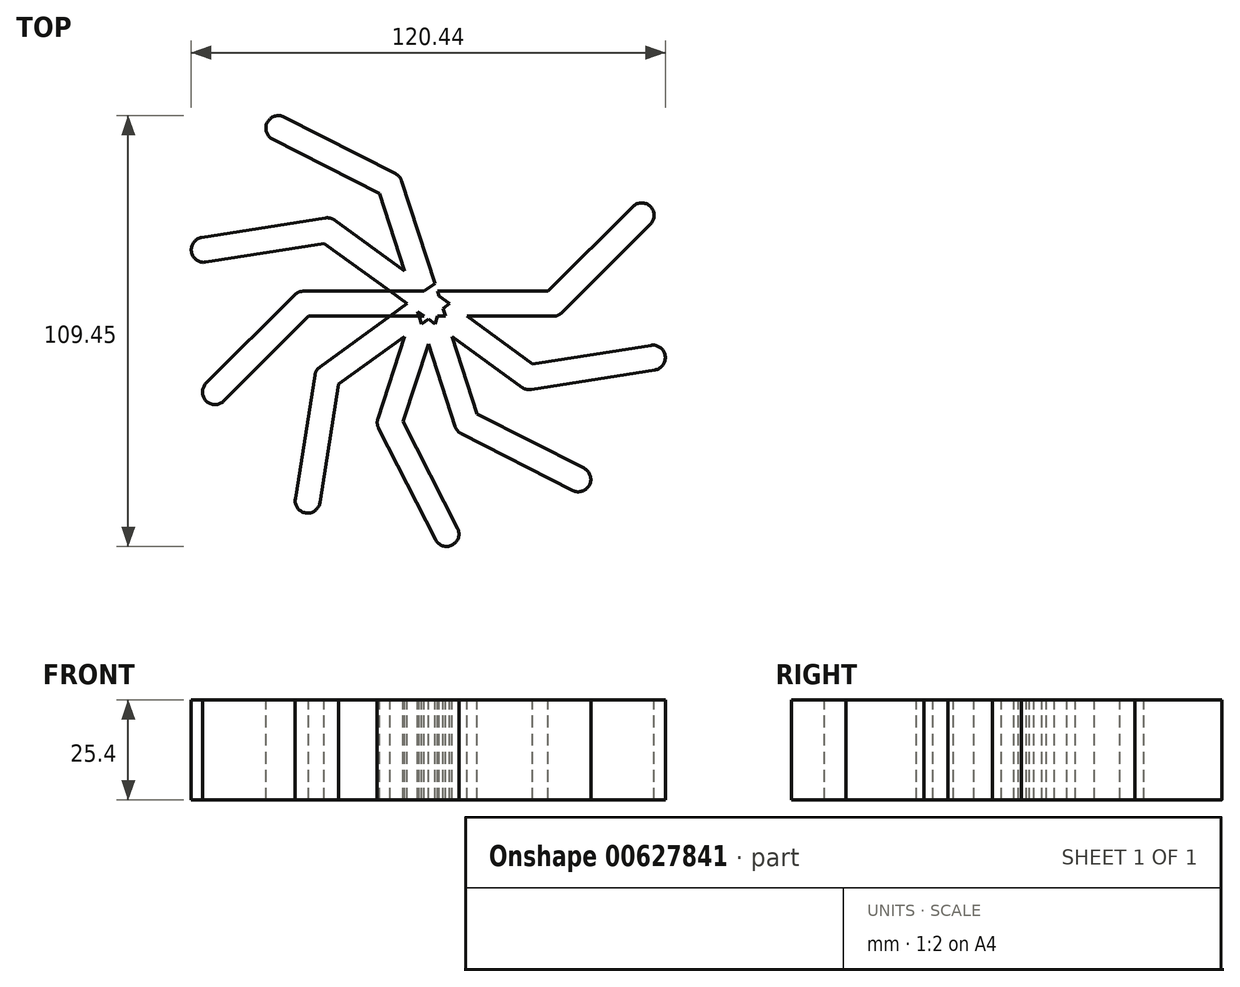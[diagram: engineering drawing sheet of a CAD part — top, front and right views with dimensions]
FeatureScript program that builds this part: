
annotation { "Feature Type Name" : "Feature", "Feature Type Description" : "" }
export const myFeature = defineFeature(function(context is Context, id is Id, definition is map)
    precondition{}
    {
        {
            var Q0;
            Q0=qCreatedBy(makeId("Top.planeOp"),FACE);
            var sketch = newSketch(context, id + "F0", { "sketchPlane" : qUnion([Q0])});
            skArc(sketch, "E0", {"start": v(31.75, -3.18) * mm, "mid": v(32.97, -2.93) * mm, "end": v(34, -2.25) * mm});
            skLineSegment(sketch, "E1", {"start": v(0, 0) * mm, "end": v(31.75, 0) * mm, "construction": true});
            skLineSegment(sketch, "E2", {"start": v(31.75, 0) * mm, "end": v(54.2, 22.45) * mm, "construction": true});
            skArc(sketch, "E3", {"start": v(56.45, 20.2) * mm, "mid": v(56.45, 24.7) * mm, "end": v(51.96, 24.7) * mm});
            skLineSegment(sketch, "E4", {"start": v(0, 3.17) * mm, "end": v(30.43, 3.17) * mm});
            skLineSegment(sketch, "E5", {"start": v(51.96, 24.7) * mm, "end": v(30.43, 3.17) * mm});
            skLineSegment(sketch, "E6", {"start": v(0, -3.18) * mm, "end": v(31.75, -3.18) * mm});
            skLineSegment(sketch, "E7", {"start": v(56.45, 20.2) * mm, "end": v(34, -2.25) * mm});
            skLineSegment(sketch, "E8.1.0", {"start": v(25.69, 18.66) * mm, "end": v(30.65, 50.02) * mm, "construction": true});
            skLineSegment(sketch, "E8.1.1", {"start": v(-1.03, 3.17) * mm, "end": v(22.76, 20.46) * mm});
            skLineSegment(sketch, "E8.1.2", {"start": v(0, 0) * mm, "end": v(25.69, 18.66) * mm, "construction": true});
            skLineSegment(sketch, "E8.1.3", {"start": v(33.79, 49.52) * mm, "end": v(28.82, 18.17) * mm});
            skLineSegment(sketch, "E8.1.4", {"start": v(1.87, -2.57) * mm, "end": v(27.55, 16.1) * mm});
            skLineSegment(sketch, "E8.1.5", {"start": v(27.52, 50.52) * mm, "end": v(22.76, 20.46) * mm});
            skArc(sketch, "E8.1.8", {"start": v(27.55, 16.1) * mm, "mid": v(28.4, 17) * mm, "end": v(28.82, 18.17) * mm});
            skLineSegment(sketch, "E8.2.0", {"start": v(9.81, 30.2) * mm, "end": v(-4.6, 58.49) * mm, "construction": true});
            skLineSegment(sketch, "E8.2.1", {"start": v(-2.7, 1.96) * mm, "end": v(6.39, 29.93) * mm});
            skLineSegment(sketch, "E8.2.2", {"start": v(0.98, 3.02) * mm, "end": v(9.81, 30.2) * mm, "construction": true});
            skLineSegment(sketch, "E8.2.3", {"start": v(-1.77, 59.93) * mm, "end": v(12.64, 31.64) * mm});
            skLineSegment(sketch, "E8.2.4", {"start": v(3.02, -0.98) * mm, "end": v(3.34, 0) * mm});
            skLineSegment(sketch, "E8.2.5", {"start": v(-7.43, 57.04) * mm, "end": v(6.39, 29.93) * mm});
            skArc(sketch, "E8.2.6", {"start": v(-3.02, 0.98) * mm, "mid": v(-0.98, -3.02) * mm, "end": v(3.02, -0.98) * mm});
            skArc(sketch, "E8.2.7", {"start": v(-1.77, 59.93) * mm, "mid": v(-6.04, 61.31) * mm, "end": v(-7.43, 57.04) * mm});
            skArc(sketch, "E8.2.8", {"start": v(12.83, 29.21) * mm, "mid": v(12.98, 30.45) * mm, "end": v(12.64, 31.64) * mm});
            skLineSegment(sketch, "E8.3.0", {"start": v(-9.81, 30.2) * mm, "end": v(-38.1, 44.61) * mm, "construction": true});
            skLineSegment(sketch, "E8.3.2", {"start": v(-0.98, 3.02) * mm, "end": v(-9.81, 30.2) * mm, "construction": true});
            skLineSegment(sketch, "E8.3.3", {"start": v(-36.66, 47.44) * mm, "end": v(-8.37, 33.02) * mm});
            skLineSegment(sketch, "E8.3.4", {"start": v(3.02, 0.98) * mm, "end": v(-6.8, 31.18) * mm});
            skLineSegment(sketch, "E8.3.5", {"start": v(-39.54, 41.78) * mm, "end": v(-12.42, 27.96) * mm});
            skArc(sketch, "E8.3.6", {"start": v(-3.02, -0.98) * mm, "mid": v(0.98, -3.02) * mm, "end": v(3.02, 0.98) * mm});
            skArc(sketch, "E8.3.7", {"start": v(-36.66, 47.44) * mm, "mid": v(-40.93, 46.05) * mm, "end": v(-39.54, 41.78) * mm});
            skArc(sketch, "E8.3.8", {"start": v(-6.8, 31.18) * mm, "mid": v(-7.4, 32.26) * mm, "end": v(-8.37, 33.02) * mm});
            skLineSegment(sketch, "E8.4.0", {"start": v(-25.69, 18.66) * mm, "end": v(-57.05, 13.7) * mm, "construction": true});
            skLineSegment(sketch, "E8.4.1", {"start": v(-1.87, -2.57) * mm, "end": v(-3.73, -1.21) * mm});
            skLineSegment(sketch, "E8.4.2", {"start": v(0, 0) * mm, "end": v(-2.7, 1.96) * mm, "construction": true});
            skLineSegment(sketch, "E8.4.3", {"start": v(-57.54, 16.83) * mm, "end": v(-26.18, 21.8) * mm});
            skLineSegment(sketch, "E8.4.4", {"start": v(1.03, 3.17) * mm, "end": v(-23.82, 21.23) * mm});
            skLineSegment(sketch, "E8.4.5", {"start": v(-56.55, 10.56) * mm, "end": v(-26.49, 15.32) * mm});
            skArc(sketch, "E8.4.6", {"start": v(-1.87, -2.57) * mm, "mid": v(1.44, -2.83) * mm, "end": v(3.18, 0) * mm});
            skArc(sketch, "E8.4.7", {"start": v(-57.54, 16.83) * mm, "mid": v(-60.18, 13.2) * mm, "end": v(-56.55, 10.56) * mm});
            skArc(sketch, "E8.4.8", {"start": v(-23.82, 21.23) * mm, "mid": v(-24.95, 21.75) * mm, "end": v(-26.18, 21.8) * mm});
            skLineSegment(sketch, "E8.5.0", {"start": v(-31.75, 0) * mm, "end": v(-54.2, -22.45) * mm, "construction": true});
            skLineSegment(sketch, "E8.5.1", {"start": v(0, -3.17) * mm, "end": v(-30.43, -3.17) * mm});
            skLineSegment(sketch, "E8.5.2", {"start": v(0, 0) * mm, "end": v(-3.34, 0) * mm, "construction": true});
            skLineSegment(sketch, "E8.5.3", {"start": v(-56.45, -20.2) * mm, "end": v(-34, 2.25) * mm});
            skLineSegment(sketch, "E8.5.4", {"start": v(0, 3.18) * mm, "end": v(-31.75, 3.18) * mm});
            skLineSegment(sketch, "E8.5.5", {"start": v(-51.96, -24.7) * mm, "end": v(-30.43, -3.17) * mm});
            skArc(sketch, "E8.5.6", {"start": v(0, -3.18) * mm, "mid": v(2.25, -2.25) * mm, "end": v(3.18, 0) * mm});
            skArc(sketch, "E8.5.7", {"start": v(-56.45, -20.2) * mm, "mid": v(-56.45, -24.7) * mm, "end": v(-51.96, -24.7) * mm});
            skArc(sketch, "E8.5.8", {"start": v(-31.75, 3.18) * mm, "mid": v(-32.97, 2.93) * mm, "end": v(-34, 2.25) * mm});
            skLineSegment(sketch, "E8.6.0", {"start": v(-25.69, -18.66) * mm, "end": v(-30.65, -50.02) * mm, "construction": true});
            skLineSegment(sketch, "E8.6.1", {"start": v(1.87, -2.57) * mm, "end": v(-22.76, -20.46) * mm});
            skLineSegment(sketch, "E8.6.2", {"start": v(0, 0) * mm, "end": v(-25.69, -18.66) * mm, "construction": true});
            skLineSegment(sketch, "E8.6.3", {"start": v(-33.79, -49.52) * mm, "end": v(-28.82, -18.17) * mm});
            skLineSegment(sketch, "E8.6.5", {"start": v(-27.52, -50.52) * mm, "end": v(-22.76, -20.46) * mm});
            skArc(sketch, "E8.6.6", {"start": v(1.87, -2.57) * mm, "mid": v(2.83, 1.44) * mm, "end": v(-0.98, 3.02) * mm});
            skArc(sketch, "E8.6.7", {"start": v(-33.79, -49.52) * mm, "mid": v(-31.15, -53.16) * mm, "end": v(-27.52, -50.52) * mm});
            skArc(sketch, "E8.6.8", {"start": v(-27.55, -16.1) * mm, "mid": v(-28.4, -17) * mm, "end": v(-28.82, -18.17) * mm});
            skLineSegment(sketch, "E8.7.0", {"start": v(-9.81, -30.2) * mm, "end": v(4.6, -58.49) * mm, "construction": true});
            skLineSegment(sketch, "E8.7.1", {"start": v(3.02, -0.98) * mm, "end": v(-6.39, -29.93) * mm});
            skLineSegment(sketch, "E8.7.2", {"start": v(-0.98, -3.02) * mm, "end": v(-9.81, -30.2) * mm, "construction": true});
            skLineSegment(sketch, "E8.7.3", {"start": v(1.77, -59.93) * mm, "end": v(-12.64, -31.64) * mm});
            skLineSegment(sketch, "E8.7.4", {"start": v(-3.02, 0.98) * mm, "end": v(-3.34, 0) * mm});
            skLineSegment(sketch, "E8.7.5", {"start": v(7.43, -57.04) * mm, "end": v(-6.39, -29.93) * mm});
            skArc(sketch, "E8.7.7", {"start": v(1.77, -59.93) * mm, "mid": v(6.04, -61.31) * mm, "end": v(7.43, -57.04) * mm});
            skArc(sketch, "E8.7.8", {"start": v(-12.83, -29.21) * mm, "mid": v(-12.98, -30.45) * mm, "end": v(-12.64, -31.64) * mm});
            skLineSegment(sketch, "E8.8.0", {"start": v(9.81, -30.2) * mm, "end": v(38.1, -44.61) * mm, "construction": true});
            skLineSegment(sketch, "E8.8.1", {"start": v(3.34, 0) * mm, "end": v(12.42, -27.96) * mm});
            skLineSegment(sketch, "E8.8.2", {"start": v(1.03, -3.18) * mm, "end": v(9.81, -30.2) * mm, "construction": true});
            skLineSegment(sketch, "E8.8.3", {"start": v(36.66, -47.44) * mm, "end": v(8.37, -33.02) * mm});
            skLineSegment(sketch, "E8.8.4", {"start": v(-3.02, -0.98) * mm, "end": v(6.8, -31.18) * mm});
            skLineSegment(sketch, "E8.8.5", {"start": v(39.54, -41.78) * mm, "end": v(12.42, -27.96) * mm});
            skArc(sketch, "E8.8.6", {"start": v(3.02, 0.98) * mm, "mid": v(1.87, 2.57) * mm, "end": v(0, 3.18) * mm});
            skArc(sketch, "E8.8.7", {"start": v(36.66, -47.44) * mm, "mid": v(40.93, -46.05) * mm, "end": v(39.54, -41.78) * mm});
            skArc(sketch, "E8.8.8", {"start": v(6.8, -31.18) * mm, "mid": v(7.4, -32.26) * mm, "end": v(8.37, -33.02) * mm});
            skLineSegment(sketch, "E8.9.0", {"start": v(25.69, -18.66) * mm, "end": v(57.05, -13.7) * mm, "construction": true});
            skLineSegment(sketch, "E8.9.1", {"start": v(1.87, 2.57) * mm, "end": v(26.49, -15.32) * mm});
            skLineSegment(sketch, "E8.9.2", {"start": v(0, 0) * mm, "end": v(25.69, -18.66) * mm, "construction": true});
            skLineSegment(sketch, "E8.9.3", {"start": v(57.54, -16.83) * mm, "end": v(26.18, -21.8) * mm});
            skLineSegment(sketch, "E8.9.4", {"start": v(-1.87, -2.57) * mm, "end": v(23.82, -21.23) * mm});
            skLineSegment(sketch, "E8.9.5", {"start": v(56.55, -10.56) * mm, "end": v(26.49, -15.32) * mm});
            skArc(sketch, "E8.9.6", {"start": v(1.87, 2.57) * mm, "mid": v(0.5, 3.14) * mm, "end": v(-0.98, 3.02) * mm});
            skArc(sketch, "E8.9.7", {"start": v(57.54, -16.83) * mm, "mid": v(60.18, -13.2) * mm, "end": v(56.55, -10.56) * mm});
            skArc(sketch, "E8.9.8", {"start": v(23.82, -21.23) * mm, "mid": v(24.95, -21.75) * mm, "end": v(26.18, -21.8) * mm});
            skPoint(sketch, "E8.center", {"position": v(0, 0) * mm});
            skLineSegment(sketch, "E9.trimOffspring", {"start": v(-5.4, 0) * mm, "end": v(-27.55, -16.1) * mm});
            skLineSegment(sketch, "E10.trimOffspring", {"start": v(-4.37, 3.18) * mm, "end": v(-12.42, 27.96) * mm});
            skLineSegment(sketch, "E11.trimOffspring", {"start": v(-5.4, 0) * mm, "end": v(-31.75, 0) * mm, "construction": true});
            skLineSegment(sketch, "E12.trimOffspring", {"start": v(-6.04, -8.31) * mm, "end": v(-12.83, -29.21) * mm});
            skArc(sketch, "E13.trimOffspring", {"start": v(-3.02, -0.98) * mm, "mid": v(-1.87, -2.57) * mm, "end": v(0, -3.18) * mm});
            skArc(sketch, "E14.trimOffspring", {"start": v(-3.02, 0.98) * mm, "mid": v(-3.14, 0.5) * mm, "end": v(-3.18, 0) * mm});
            skLineSegment(sketch, "E15.trimOffspring", {"start": v(-4.37, 3.17) * mm, "end": v(-25.69, 18.66) * mm, "construction": true});
            skArc(sketch, "E16.trimOffspring", {"start": v(0.98, 3.02) * mm, "mid": v(0.5, 3.14) * mm, "end": v(0, 3.18) * mm});
            skArc(sketch, "E17.trimOffspring", {"start": v(-3.18, 0) * mm, "mid": v(-2.83, -1.44) * mm, "end": v(-1.87, -2.57) * mm});
            skLineSegment(sketch, "E18.trimOffspring", {"start": v(-5.4, 0) * mm, "end": v(-26.49, 15.32) * mm});
            skArc(sketch, "E19.trimOffspring", {"start": v(3.02, 0.98) * mm, "mid": v(2.57, 1.87) * mm, "end": v(1.87, 2.57) * mm});
            skSolve(sketch);
        }
        {
            var Q0;
            Q0=makeQuery(id+"F0.imprint","IMPRINT",FACE,{"disambiguationData":[TD([[makeQuery(id+"F0.imprint","IMPRINT",EDGE,{"derivedFrom":sQuery(id+"F0.wireOp",EDGE,"E8.7.3")}),-1.0]])]});
            var Q1;
            Q1=makeQuery(id+"F0.imprint","IMPRINT",FACE,{"disambiguationData":[TD([[makeQuery(id+"F0.imprint","IMPRINT",EDGE,{"derivedFrom":sQuery(id+"F0.wireOp",EDGE,"E8.8.3")}),-1.0]])]});
            var Q2;
            Q2=makeQuery(id+"F0.imprint","IMPRINT",FACE,{"disambiguationData":[TD([[makeQuery(id+"F0.imprint","IMPRINT",EDGE,{"derivedFrom":sQuery(id+"F0.wireOp",EDGE,"E8.9.3")}),-1.0]])]});
            var Q3;
            {var subQ5=sQuery(id+"F0.wireOp",EDGE,"E0");Q3=makeQuery(id+"F0.imprint","IMPRINT",FACE,{"disambiguationData":[TD([[makeQuery(id+"F0.imprint","IMPRINT",EDGE,{"derivedFrom":subQ5}),1.0]])]});}
            var Q4;
            Q4=makeQuery(id+"F0.imprint","IMPRINT",FACE,{"disambiguationData":[TD([[makeQuery(id+"F0.imprint","IMPRINT",EDGE,{"derivedFrom":sQuery(id+"F0.wireOp",EDGE,"E8.1.3")}),-1.0]])]});
            var Q5;
            Q5=makeQuery(id+"F0.imprint","IMPRINT",FACE,{"disambiguationData":[TD([[makeQuery(id+"F0.imprint","IMPRINT",EDGE,{"derivedFrom":sQuery(id+"F0.wireOp",EDGE,"E8.2.3")}),-1.0]])]});
            var Q6;
            Q6=makeQuery(id+"F0.imprint","IMPRINT",FACE,{"disambiguationData":[TD([[makeQuery(id+"F0.imprint","IMPRINT",EDGE,{"derivedFrom":sQuery(id+"F0.wireOp",EDGE,"E8.3.3")}),-1.0]])]});
            var Q7;
            Q7=makeQuery(id+"F0.imprint","IMPRINT",FACE,{"disambiguationData":[TD([[makeQuery(id+"F0.imprint","IMPRINT",EDGE,{"derivedFrom":sQuery(id+"F0.wireOp",EDGE,"E8.4.3")}),-1.0]])]});
            var Q8;
            Q8=makeQuery(id+"F0.imprint","IMPRINT",FACE,{"disambiguationData":[TD([[makeQuery(id+"F0.imprint","IMPRINT",EDGE,{"derivedFrom":sQuery(id+"F0.wireOp",EDGE,"E8.5.3")}),-1.0]])]});
            var Q9;
            Q9=makeQuery(id+"F0.imprint","IMPRINT",FACE,{"disambiguationData":[TD([[makeQuery(id+"F0.imprint","IMPRINT",EDGE,{"derivedFrom":sQuery(id+"F0.wireOp",EDGE,"E8.6.3")}),-1.0]])]});
            var Q10;
            {var subQ3=sQuery(id+"F0.wireOp",EDGE,"E8.4.6");Q10=makeQuery(id+"F0.imprint","IMPRINT",FACE,{"disambiguationData":[TD([[makeQuery(id+"F0.imprint","IMPRINT",EDGE,{"derivedFrom":subQ3}),1.0]])]});}
            var Q11;
            {var subQ0=sQuery(id+"F0.wireOp",EDGE,"E8.4.4");var subQ1=sQuery(id+"F0.wireOp",EDGE,"E8.1.1");var subQ2=makeQuery(id+"F0.imprint","INTERSECT",VERTEX,{"derivedFrom":[subQ1,subQ0]});Q11=makeQuery(id+"F0.imprint","IMPRINT",FACE,{"disambiguationData":[TD([[makeQuery(id+"F0.imprint","IMPRINT",EDGE,{"disambiguationData":[TD([[subQ2,-1.0]])],"derivedFrom":subQ1}),1.0]])]});}
            var Q12;
            {var subQ0=sQuery(id+"F0.wireOp",EDGE,"E8.3.4");var subQ1=sQuery(id+"F0.wireOp",EDGE,"E4");var subQ2=makeQuery(id+"F0.imprint","INTERSECT",VERTEX,{"derivedFrom":[subQ1,subQ0]});Q12=makeQuery(id+"F0.imprint","IMPRINT",FACE,{"disambiguationData":[TD([[makeQuery(id+"F0.imprint","IMPRINT",EDGE,{"disambiguationData":[TD([[subQ2,-1.0]])],"derivedFrom":subQ1}),1.0]])]});}
            var Q13;
            {var subQ0=sQuery(id+"F0.wireOp",EDGE,"E8.1.4");var subQ1=sQuery(id+"F0.wireOp",EDGE,"E4");var subQ2=makeQuery(id+"F0.imprint","INTERSECT",VERTEX,{"derivedFrom":[subQ1,subQ0]});Q13=makeQuery(id+"F0.imprint","IMPRINT",FACE,{"disambiguationData":[TD([[makeQuery(id+"F0.imprint","IMPRINT",EDGE,{"disambiguationData":[TD([[subQ2,1.0]])],"derivedFrom":subQ1}),-1.0]])]});}
            var Q14;
            {var subQ0=sQuery(id+"F0.wireOp",EDGE,"E8.9.1");var subQ1=sQuery(id+"F0.wireOp",EDGE,"E6");var subQ2=makeQuery(id+"F0.imprint","INTERSECT",VERTEX,{"derivedFrom":[subQ1,subQ0]});Q14=makeQuery(id+"F0.imprint","IMPRINT",FACE,{"disambiguationData":[TD([[makeQuery(id+"F0.imprint","IMPRINT",EDGE,{"disambiguationData":[TD([[subQ2,1.0]])],"derivedFrom":subQ1}),1.0]])]});}
            var Q15;
            {var subQ0=sQuery(id+"F0.wireOp",EDGE,"E8.7.1");var subQ1=sQuery(id+"F0.wireOp",EDGE,"E6");var subQ2=makeQuery(id+"F0.imprint","INTERSECT",VERTEX,{"derivedFrom":[subQ1,subQ0]});Q15=makeQuery(id+"F0.imprint","IMPRINT",FACE,{"disambiguationData":[TD([[makeQuery(id+"F0.imprint","IMPRINT",EDGE,{"disambiguationData":[TD([[subQ2,-1.0]])],"derivedFrom":subQ1}),-1.0]])]});}
            var Q16;
            {var subQ0=sQuery(id+"F0.wireOp",EDGE,"E8.9.4");var subQ1=sQuery(id+"F0.wireOp",EDGE,"E8.6.1");var subQ2=makeQuery(id+"F0.imprint","INTERSECT",VERTEX,{"derivedFrom":[subQ1,subQ0]});Q16=makeQuery(id+"F0.imprint","IMPRINT",FACE,{"disambiguationData":[TD([[makeQuery(id+"F0.imprint","IMPRINT",EDGE,{"disambiguationData":[TD([[subQ2,-1.0]])],"derivedFrom":subQ1}),1.0]])]});}
            var Q17;
            {var subQ0=sQuery(id+"F0.wireOp",EDGE,"E8.8.4");var subQ1=sQuery(id+"F0.wireOp",EDGE,"E8.5.1");var subQ2=makeQuery(id+"F0.imprint","INTERSECT",VERTEX,{"derivedFrom":[subQ1,subQ0]});Q17=makeQuery(id+"F0.imprint","IMPRINT",FACE,{"disambiguationData":[TD([[makeQuery(id+"F0.imprint","IMPRINT",EDGE,{"disambiguationData":[TD([[subQ2,-1.0]])],"derivedFrom":subQ1}),1.0]])]});}
            var Q18;
            {var subQ0=sQuery(id+"F0.wireOp",EDGE,"E8.7.4");var subQ1=sQuery(id+"F0.wireOp",EDGE,"E8.4.1");var subQ2=makeQuery(id+"F0.imprint","INTERSECT",VERTEX,{"derivedFrom":[subQ1,subQ0]});Q18=makeQuery(id+"F0.imprint","IMPRINT",FACE,{"disambiguationData":[TD([[makeQuery(id+"F0.imprint","IMPRINT",EDGE,{"disambiguationData":[TD([[subQ2,-1.0]])],"derivedFrom":subQ1}),1.0]])]});}
            var Q19;
            {var subQ0=sQuery(id+"F0.wireOp",EDGE,"E8.6.4");var subQ1=sQuery(id+"F0.wireOp",EDGE,"E8.3.1");var subQ2=makeQuery(id+"F0.imprint","INTERSECT",VERTEX,{"derivedFrom":[subQ1,subQ0]});Q19=makeQuery(id+"F0.imprint","IMPRINT",FACE,{"disambiguationData":[TD([[makeQuery(id+"F0.imprint","IMPRINT",EDGE,{"disambiguationData":[TD([[subQ2,-1.0]])],"derivedFrom":subQ1}),1.0]])]});}
            var Q20;
            {var subQ0=sQuery(id+"F0.wireOp",EDGE,"E8.5.4");var subQ1=sQuery(id+"F0.wireOp",EDGE,"E8.2.1");var subQ2=makeQuery(id+"F0.imprint","INTERSECT",VERTEX,{"derivedFrom":[subQ1,subQ0]});Q20=makeQuery(id+"F0.imprint","IMPRINT",FACE,{"disambiguationData":[TD([[makeQuery(id+"F0.imprint","IMPRINT",EDGE,{"disambiguationData":[TD([[subQ2,-1.0]])],"derivedFrom":subQ1}),1.0]])]});}
            var Q21;
            {var subQ0=sQuery(id+"F0.wireOp",EDGE,"E8.5.4");var subQ1=sQuery(id+"F0.wireOp",EDGE,"E8.1.1");var subQ2=makeQuery(id+"F0.imprint","INTERSECT",VERTEX,{"derivedFrom":[subQ1,subQ0]});Q21=makeQuery(id+"F0.imprint","IMPRINT",FACE,{"disambiguationData":[TD([[makeQuery(id+"F0.imprint","IMPRINT",EDGE,{"disambiguationData":[TD([[subQ2,-1.0]])],"derivedFrom":subQ1}),1.0]])]});}
            extrude(context, id + "F1", {"entities" : qUnion([Q0, Q1, Q2, Q3, Q4, Q5, Q6, Q7, Q8, Q9, Q10, Q11, Q12, Q13, Q14, Q15, Q16, Q17, Q18, Q19, Q20, Q21]), "oppositeDirection" : true, "depth" : 25.4 * mm, "offsetDistance" : 25.4 * mm});
        }
    });
